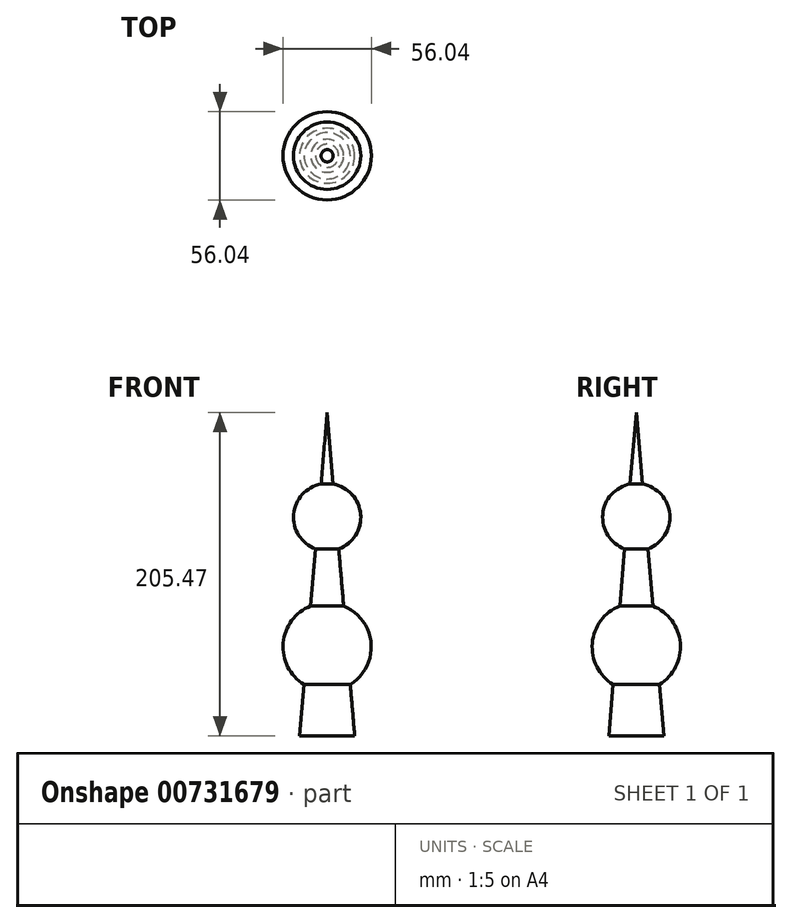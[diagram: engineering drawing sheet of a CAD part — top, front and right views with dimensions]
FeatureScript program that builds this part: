
annotation { "Feature Type Name" : "Feature", "Feature Type Description" : "" }
export const myFeature = defineFeature(function(context is Context, id is Id, definition is map)
    precondition{}
    {
        {
            var Q0;
            Q0=qCreatedBy(makeId("Front.planeOp"),FACE);
            var sketch = newSketch(context, id + "F0", { "sketchPlane" : qUnion([Q0])});
            skLineSegment(sketch, "E0", {"start": v(0, 0) * mm, "end": v(-17.48, 0) * mm});
            skLineSegment(sketch, "E1", {"start": v(-17.48, 0) * mm, "end": v(-14.7, 32.68) * mm});
            skLineSegment(sketch, "E2", {"start": v(0, 205.47) * mm, "end": v(0, 0) * mm});
            skArc(sketch, "E3", {"start": v(-3.87, 159.95) * mm, "mid": v(-21.3, 140.73) * mm, "end": v(-7.37, 118.85) * mm});
            skArc(sketch, "E4", {"start": v(-10.46, 82.53) * mm, "mid": v(-27.92, 58.9) * mm, "end": v(-14.7, 32.68) * mm});
            skLineSegment(sketch, "E5.trimOffspring", {"start": v(-3.87, 159.95) * mm, "end": v(0, 205.47) * mm});
            skLineSegment(sketch, "E6.trimOffspring", {"start": v(-10.46, 82.53) * mm, "end": v(-7.37, 118.85) * mm});
            skSolve(sketch);
        }
        {
            var Q0;
            Q0=makeQuery(id+"F0.imprint","IMPRINT",FACE,{"disambiguationData":[TD([[makeQuery(id+"F0.imprint","IMPRINT",EDGE,{"derivedFrom":sQuery(id+"F0.wireOp",EDGE,"E0")}),-1.0]])]});
            var Q1;
            Q1=sQuery(id+"F0.wireOp",EDGE,"E2");
            revolve(context, id + "F1", {"surfaceOperationType" : NewSurfaceOperationType.NEW, "entities" : qUnion([Q0]), "axis" : qUnion([Q1]), "revolveType" : RevolveType.FULL});
        }
    });
